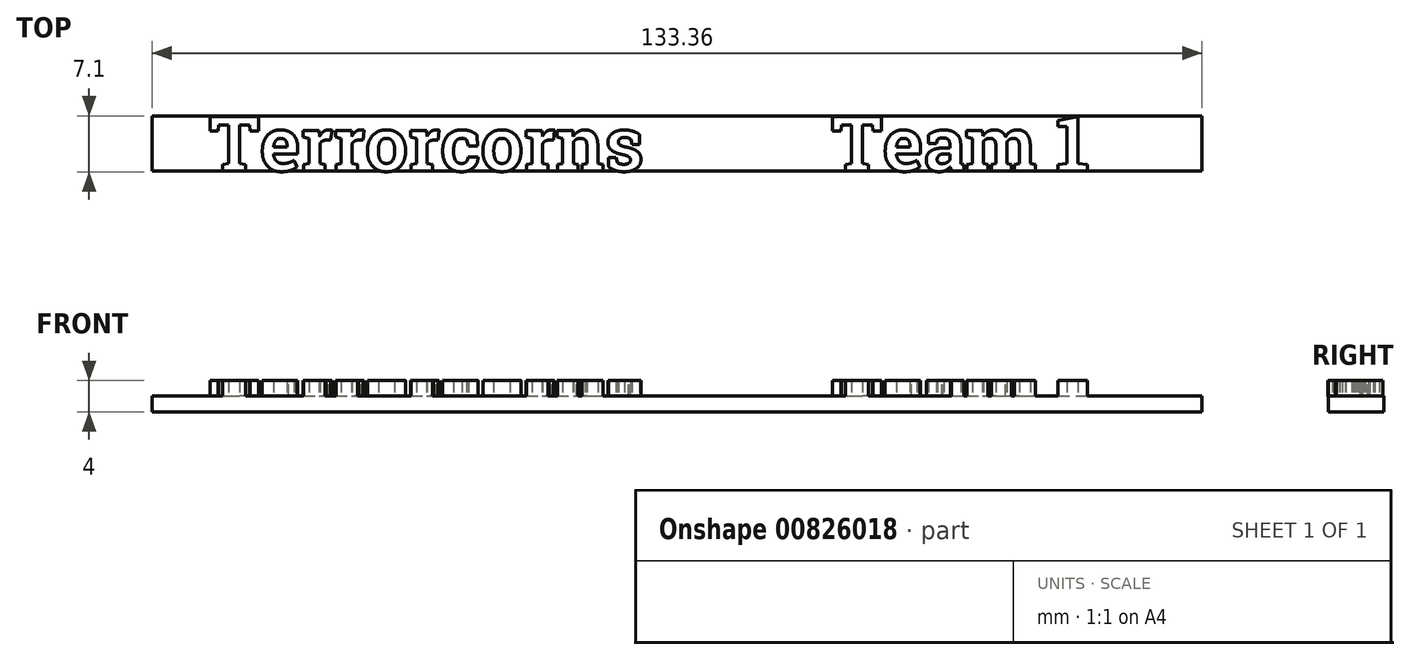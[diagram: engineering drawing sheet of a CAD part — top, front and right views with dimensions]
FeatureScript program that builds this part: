
annotation { "Feature Type Name" : "Feature", "Feature Type Description" : "" }
export const myFeature = defineFeature(function(context is Context, id is Id, definition is map)
    precondition{}
    {
        {
            var Q0;
            Q0=qCreatedBy(makeId("Top.planeOp"),FACE);
            var sketch = newSketch(context, id + "F0", { "sketchPlane" : qUnion([Q0])});
            skLineSegment(sketch, "E0.bottom", {"start": v(66.67, -3.5) * mm, "end": v(-66.67, -3.5) * mm});
            skLineSegment(sketch, "E0.top", {"start": v(66.67, 3.5) * mm, "end": v(-66.67, 3.5) * mm});
            skLineSegment(sketch, "E0.left", {"start": v(66.67, -3.5) * mm, "end": v(66.67, 3.5) * mm});
            skLineSegment(sketch, "E0.right", {"start": v(-66.67, -3.5) * mm, "end": v(-66.67, 3.5) * mm});
            skPoint(sketch, "E0.middle", {"position": v(0, 0) * mm});
            skSolve(sketch);
        }
        {
            var Q0;
            Q0 = qSketchRegion(id + "F0", true);
            extrude(context, id + "F1", {"entities" : qUnion([Q0]), "depth" : 2 * mm, "offsetDistance" : 25 * mm});
        }
        {
            var Q0;
            Q0=makeQuery(id+"F1.opExtrude","CAP_FACE",FACE,{"disambiguationData":[OSD([sQuery(id+"F0.wireOp",EDGE,"E0.bottom"),sQuery(id+"F0.wireOp",EDGE,"E0.top"),sQuery(id+"F0.wireOp",EDGE,"E0.left"),sQuery(id+"F0.wireOp",EDGE,"E0.right")])],"isStart":false});
            var sketch = newSketch(context, id + "F2", { "sketchPlane" : qUnion([Q0])});
            skText(sketch, "E1", { "text": "   Terrorcorns          Team 1", "fontName": "RobotoSlab-Bold.ttf"});
            const initialGuessF2  = {"E1": [-0.06667, -0.0035, 1, 0, 0.007]};
            skSetInitialGuess(sketch, initialGuessF2);
            skSolve(sketch);
        }
        {
            var Q0;
            Q0 = qSketchRegion(id + "F2", true);
            extrude(context, id + "F3", {"entities" : qUnion([Q0]), "operationType" : NewBodyOperationType.ADD, "depth" : 2 * mm, "offsetDistance" : 25 * mm});
        }
    });
